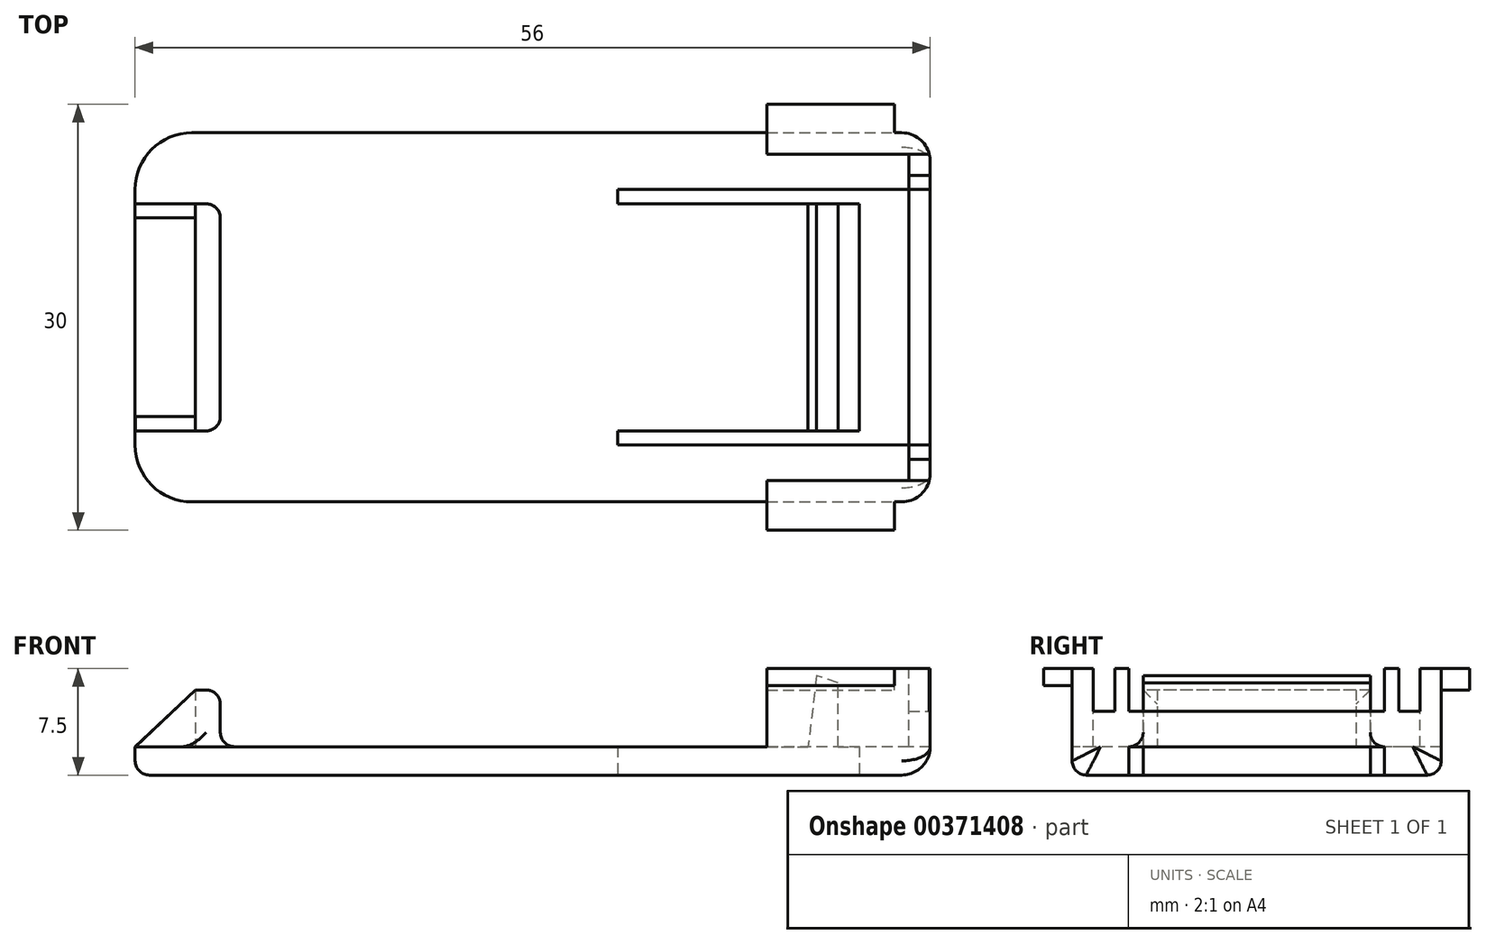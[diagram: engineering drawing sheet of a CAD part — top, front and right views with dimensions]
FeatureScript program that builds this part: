
annotation { "Feature Type Name" : "Feature", "Feature Type Description" : "" }
export const myFeature = defineFeature(function(context is Context, id is Id, definition is map)
    precondition{}
    {
        {
            var Q0;
            Q0=qCreatedBy(makeId("Top.planeOp"),FACE);
            var sketch = newSketch(context, id + "F0", { "sketchPlane" : qUnion([Q0])});
            skLineSegment(sketch, "E0.bottom", {"start": v(28, 13) * mm, "end": v(-24, 13) * mm});
            skLineSegment(sketch, "E0.top", {"start": v(28, -13) * mm, "end": v(-24, -13) * mm});
            skLineSegment(sketch, "E0.left", {"start": v(28, 13) * mm, "end": v(28, 9) * mm});
            skLineSegment(sketch, "E0.right", {"start": v(-28, 9) * mm, "end": v(-28, -9) * mm});
            skPoint(sketch, "E0.middle", {"position": v(0, 0) * mm});
            skLineSegment(sketch, "E1.bottom", {"start": v(28, 9) * mm, "end": v(6, 9) * mm});
            skLineSegment(sketch, "E1.top", {"start": v(28, -9) * mm, "end": v(6, -9) * mm});
            skLineSegment(sketch, "E1.right", {"start": v(6, 9) * mm, "end": v(6, 8) * mm});
            skLineSegment(sketch, "E2.trimOffspring", {"start": v(28, -9) * mm, "end": v(28, -13) * mm});
            skLineSegment(sketch, "E3.bottom", {"start": v(6, 8) * mm, "end": v(23, 8) * mm});
            skLineSegment(sketch, "E3.top", {"start": v(6, -8) * mm, "end": v(23, -8) * mm});
            skLineSegment(sketch, "E3.right", {"start": v(23, 8) * mm, "end": v(23, -8) * mm});
            skLineSegment(sketch, "E4.trimOffspring", {"start": v(6, -8) * mm, "end": v(6, -9) * mm});
            skPoint(sketch, "E5.visualSharp", {"position": v(-28, 13) * mm});
            skArc(sketch, "E5.filletArc", {"start": v(-24, 13) * mm, "mid": v(-26.83, 11.83) * mm, "end": v(-28, 9) * mm});
            skPoint(sketch, "E6.visualSharp", {"position": v(-28, -13) * mm});
            skArc(sketch, "E6.filletArc", {"start": v(-28, -9) * mm, "mid": v(-26.83, -11.83) * mm, "end": v(-24, -13) * mm});
            skSolve(sketch);
        }
        {
            var Q0;
            Q0=makeQuery(id+"F0.imprint","IMPRINT",FACE,{"disambiguationData":[TD([[makeQuery(id+"F0.imprint","IMPRINT",EDGE,{"derivedFrom":sQuery(id+"F0.wireOp",EDGE,"E0.bottom")}),1.0]])]});
            extrude(context, id + "F1", {"entities" : qUnion([Q0]), "depth" : 2 * mm});
        }
        {
            var Q0;
            Q0=makeQuery(id+"F1.opExtrude","CAP_FACE",FACE,{"disambiguationData":[OSD([sQuery(id+"F0.wireOp",EDGE,"E0.bottom"),sQuery(id+"F0.wireOp",EDGE,"E0.top"),sQuery(id+"F0.wireOp",EDGE,"E0.left"),sQuery(id+"F0.wireOp",EDGE,"E0.right"),sQuery(id+"F0.wireOp",EDGE,"E1.bottom"),sQuery(id+"F0.wireOp",EDGE,"E1.top"),sQuery(id+"F0.wireOp",EDGE,"E1.right"),sQuery(id+"F0.wireOp",EDGE,"E2.trimOffspring"),sQuery(id+"F0.wireOp",EDGE,"E3.bottom"),sQuery(id+"F0.wireOp",EDGE,"E3.top"),sQuery(id+"F0.wireOp",EDGE,"E3.right"),sQuery(id+"F0.wireOp",EDGE,"E4.trimOffspring"),sQuery(id+"F0.wireOp",EDGE,"E5.filletArc"),sQuery(id+"F0.wireOp",EDGE,"E6.filletArc")])],"isStart":false});
            var sketch = newSketch(context, id + "F2", { "sketchPlane" : qUnion([Q0])});
            skLineSegment(sketch, "E7.bottom", {"start": v(-23.75, 8) * mm, "end": v(-22, 8) * mm});
            skLineSegment(sketch, "E7.top", {"start": v(-23.75, -8) * mm, "end": v(-22, -8) * mm});
            skLineSegment(sketch, "E7.left", {"start": v(-23.75, 8) * mm, "end": v(-23.75, -8) * mm});
            skLineSegment(sketch, "E7.right", {"start": v(-22, 8) * mm, "end": v(-22, -8) * mm});
            skSolve(sketch);
        }
        {
            var Q0;
            Q0=makeQuery(id+"F2.imprint","IMPRINT",FACE,{"disambiguationData":[TD([[makeQuery(id+"F2.imprint","IMPRINT",EDGE,{"derivedFrom":sQuery(id+"F2.wireOp",EDGE,"E7.bottom")}),-1.0]])]});
            extrude(context, id + "F3", {"entities" : qUnion([Q0]), "operationType" : NewBodyOperationType.ADD, "depth" : 4 * mm});
        }
        {
            var Q0;
            Q0=makeQuery(id+"F3.opExtrude","SWEPT_FACE",FACE,{"disambiguationData":[OSD([sQuery(id+"F2.wireOp",EDGE,"E7.top")])]});
            var sketch = newSketch(context, id + "F4", { "sketchPlane" : qUnion([Q0])});
            skLineSegment(sketch, "E8", {"start": v(-23.75, 6) * mm, "end": v(-27.98, 2) * mm});
            skLineSegment(sketch, "E9", {"start": v(-27.98, 2) * mm, "end": v(-23.75, 2) * mm});
            skLineSegment(sketch, "E10", {"start": v(-23.75, 2) * mm, "end": v(-23.75, 6) * mm});
            skSolve(sketch);
        }
        {
            var Q0;
            Q0=makeQuery(id+"F4.imprint","IMPRINT",FACE,{"disambiguationData":[TD([[makeQuery(id+"F4.imprint","IMPRINT",EDGE,{"derivedFrom":sQuery(id+"F4.wireOp",EDGE,"E8")}),1.0]])]});
            extrude(context, id + "F5", {"entities" : qUnion([Q0]), "operationType" : NewBodyOperationType.ADD, "oppositeDirection" : true, "depth" : 1 * mm});
        }
        {
            var Q0;
            Q0=makeQuery(id+"F3.opExtrude","SWEPT_FACE",FACE,{"disambiguationData":[OSD([sQuery(id+"F2.wireOp",EDGE,"E7.bottom")])]});
            var sketch = newSketch(context, id + "F6", { "sketchPlane" : qUnion([Q0])});
            skLineSegment(sketch, "E11", {"start": v(23.75, 2) * mm, "end": v(23.75, 6) * mm});
            skLineSegment(sketch, "E12.MirrorCS", {"start": v(28, 2) * mm, "end": v(23.75, 2) * mm});
            skLineSegment(sketch, "E13.MirrorCS", {"start": v(23.75, 6) * mm, "end": v(28, 2) * mm});
            skSolve(sketch);
        }
        {
            var Q0;
            {var subQ6=sQuery(id+"F6.wireOp",EDGE,"E13.MirrorCS");Q0=makeQuery(id+"F6.imprint","IMPRINT",FACE,{"disambiguationData":[TD([[makeQuery(id+"F6.imprint","IMPRINT",EDGE,{"derivedFrom":subQ6}),-1.0]])]});}
            extrude(context, id + "F7", {"entities" : qUnion([Q0]), "operationType" : NewBodyOperationType.ADD, "oppositeDirection" : true, "depth" : 1 * mm});
        }
        {
            var Q0;
            Q0=makeQuery(id+"F1.opExtrude","SWEPT_FACE",FACE,{"disambiguationData":[OSD([sQuery(id+"F0.wireOp",EDGE,"E3.top")])]});
            var sketch = newSketch(context, id + "F8", { "sketchPlane" : qUnion([Q0])});
            skLineSegment(sketch, "E14", {"start": v(21.5, 2) * mm, "end": v(21.5, 6.5) * mm});
            skLineSegment(sketch, "E15", {"start": v(21.5, 6.5) * mm, "end": v(20, 7) * mm});
            skLineSegment(sketch, "E16", {"start": v(20, 7) * mm, "end": v(19.4, 2) * mm});
            skLineSegment(sketch, "E17", {"start": v(19.4, 2) * mm, "end": v(21.5, 2) * mm});
            skSolve(sketch);
        }
        {
            var Q0;
            Q0=makeQuery(id+"F1.opExtrude","SWEPT_FACE",FACE,{"disambiguationData":[OSD([sQuery(id+"F0.wireOp",EDGE,"E0.top")])]});
            var sketch = newSketch(context, id + "F9", { "sketchPlane" : qUnion([Q0])});
            skLineSegment(sketch, "E18.bottom", {"start": v(16.5, 2) * mm, "end": v(28, 2) * mm});
            skLineSegment(sketch, "E18.top", {"start": v(16.5, 7.5) * mm, "end": v(28, 7.5) * mm});
            skLineSegment(sketch, "E18.left", {"start": v(16.5, 2) * mm, "end": v(16.5, 7.5) * mm});
            skLineSegment(sketch, "E18.right", {"start": v(28, 2) * mm, "end": v(28, 7.5) * mm});
            skSolve(sketch);
        }
        {
            var Q0;
            Q0=makeQuery(id+"F9.imprint","IMPRINT",FACE,{"disambiguationData":[TD([[makeQuery(id+"F9.imprint","IMPRINT",EDGE,{"derivedFrom":sQuery(id+"F9.wireOp",EDGE,"E18.bottom")}),-1.0]])]});
            extrude(context, id + "F10", {"entities" : qUnion([Q0]), "operationType" : NewBodyOperationType.ADD, "oppositeDirection" : true, "depth" : 26 * mm});
        }
        {
            var Q0;
            Q0=makeQuery(id+"F10.opExtrude","SWEPT_FACE",FACE,{"disambiguationData":[OSD([sQuery(id+"F9.wireOp",EDGE,"E18.top")])]});
            var sketch = newSketch(context, id + "F11", { "sketchPlane" : qUnion([Q0])});
            skLineSegment(sketch, "E19.bottom", {"start": v(28, -11.5) * mm, "end": v(16.5, -11.5) * mm});
            skLineSegment(sketch, "E19.top", {"start": v(28, 11.5) * mm, "end": v(16.5, 11.5) * mm});
            skLineSegment(sketch, "E19.left", {"start": v(28, -11.5) * mm, "end": v(28, 11.5) * mm});
            skLineSegment(sketch, "E19.right", {"start": v(16.5, -11.5) * mm, "end": v(16.5, 11.5) * mm});
            skSolve(sketch);
        }
        {
            var Q0;
            Q0 = qSketchRegion(id + "F11", true);
            extrude(context, id + "F12", {"entities" : qUnion([Q0]), "operationType" : NewBodyOperationType.REMOVE, "oppositeDirection" : true, "depth" : 5.5 * mm});
        }
        {
            var Q0;
            Q0=makeQuery(id+"F8.imprint","IMPRINT",FACE,{"disambiguationData":[TD([[makeQuery(id+"F8.imprint","IMPRINT",EDGE,{"derivedFrom":sQuery(id+"F8.wireOp",EDGE,"E14")}),1.0]])]});
            extrude(context, id + "F13", {"entities" : qUnion([Q0]), "operationType" : NewBodyOperationType.ADD, "oppositeDirection" : true, "depth" : 16 * mm});
        }
        {
            var Q0;
            {var subQ0=sQuery(id+"F0.wireOp",EDGE,"E0.top");var subQ2=sQuery(id+"F9.wireOp",EDGE,"E18.right");var subQ10=sQuery(id+"F0.wireOp",EDGE,"E2.trimOffspring");var subQ14=sQuery(id+"F0.wireOp",EDGE,"E0.left");Q0=makeQuery(id+"F12.boolean.opBoolean","SPLIT",FACE,{"disambiguationData":[TD([makeQuery(id+"F1.opExtrude","SWEPT_FACE",FACE,{"disambiguationData":[OSD([subQ0])]})])],"derivedFrom":makeQuery(id+"F10.boolean.opBoolean","MERGE",FACE,{"derivedFrom":[makeQuery(id+"F1.opExtrude","SWEPT_FACE",FACE,{"disambiguationData":[OSD([subQ14])]}),makeQuery(id+"F1.opExtrude","SWEPT_FACE",FACE,{"disambiguationData":[OSD([subQ10])]}),makeQuery(id+"F10.opExtrude","SWEPT_FACE",FACE,{"disambiguationData":[OSD([subQ2])]})]})});}
            var sketch = newSketch(context, id + "F14", { "sketchPlane" : qUnion([Q0])});
            skLineSegment(sketch, "E20.bottom", {"start": v(-11.5, 2) * mm, "end": v(11.5, 2) * mm});
            skLineSegment(sketch, "E20.top", {"start": v(-11.5, 4.5) * mm, "end": v(-10, 4.5) * mm});
            skLineSegment(sketch, "E20.left", {"start": v(-11.5, 2) * mm, "end": v(-11.5, 4.5) * mm});
            skLineSegment(sketch, "E20.right", {"start": v(11.5, 2) * mm, "end": v(11.5, 4.5) * mm});
            skLineSegment(sketch, "E21.top", {"start": v(-10, 7.5) * mm, "end": v(-9, 7.5) * mm});
            skLineSegment(sketch, "E21.left", {"start": v(-10, 4.5) * mm, "end": v(-10, 7.5) * mm});
            skLineSegment(sketch, "E21.right", {"start": v(-9, 4.5) * mm, "end": v(-9, 7.5) * mm});
            skLineSegment(sketch, "E22.top", {"start": v(9, 7.5) * mm, "end": v(10, 7.5) * mm});
            skLineSegment(sketch, "E22.left", {"start": v(9, 4.5) * mm, "end": v(9, 7.5) * mm});
            skLineSegment(sketch, "E22.right", {"start": v(10, 4.5) * mm, "end": v(10, 7.5) * mm});
            skLineSegment(sketch, "E23.trimOffspring", {"start": v(-9, 4.5) * mm, "end": v(9, 4.5) * mm});
            skLineSegment(sketch, "E24.trimOffspring", {"start": v(10, 4.5) * mm, "end": v(11.5, 4.5) * mm});
            skSolve(sketch);
        }
        {
            var Q0;
            Q0=makeQuery(id+"F14.imprint","IMPRINT",FACE,{"disambiguationData":[TD([[makeQuery(id+"F14.imprint","IMPRINT",EDGE,{"derivedFrom":sQuery(id+"F14.wireOp",EDGE,"E20.top")}),-1.0]])]});
            extrude(context, id + "F15", {"entities" : qUnion([Q0]), "operationType" : NewBodyOperationType.ADD, "oppositeDirection" : true, "depth" : 1.5 * mm});
        }
        {
            var Q0;
            {var subQ2=sQuery(id+"F9.wireOp",EDGE,"E18.top");Q0=makeQuery(id+"F12.boolean.opBoolean","SPLIT",FACE,{"disambiguationData":[TD([makeQuery(id+"F1.opExtrude","SWEPT_FACE",FACE,{"disambiguationData":[OSD([sQuery(id+"F0.wireOp",EDGE,"E0.top")])]})])],"derivedFrom":makeQuery(id+"F10.opExtrude","SWEPT_FACE",FACE,{"disambiguationData":[OSD([subQ2])]})});}
            var sketch = newSketch(context, id + "F16", { "sketchPlane" : qUnion([Q0])});
            skLineSegment(sketch, "E25.bottom", {"start": v(16.5, -11.5) * mm, "end": v(25.5, -11.5) * mm});
            skLineSegment(sketch, "E25.top", {"start": v(16.5, -15) * mm, "end": v(25.5, -15) * mm});
            skLineSegment(sketch, "E25.left", {"start": v(16.5, -11.5) * mm, "end": v(16.5, -15) * mm});
            skLineSegment(sketch, "E25.right", {"start": v(25.5, -11.5) * mm, "end": v(25.5, -15) * mm});
            skSolve(sketch);
        }
        {
            var Q0;
            {var subQ0=sQuery(id+"F16.wireOp",EDGE,"E25.top");Q0=makeQuery(id+"F16.imprint","IMPRINT",FACE,{"disambiguationData":[TD([[makeQuery(id+"F16.imprint","IMPRINT",EDGE,{"derivedFrom":subQ0}),1.0]])]});}
            extrude(context, id + "F17", {"entities" : qUnion([Q0]), "operationType" : NewBodyOperationType.ADD, "oppositeDirection" : true, "depth" : 1.2 * mm});
        }
        {
            var Q0;
            {var subQ2=sQuery(id+"F9.wireOp",EDGE,"E18.top");Q0=makeQuery(id+"F12.boolean.opBoolean","SPLIT",FACE,{"disambiguationData":[TD([makeQuery(id+"F1.opExtrude","SWEPT_FACE",FACE,{"disambiguationData":[OSD([sQuery(id+"F0.wireOp",EDGE,"E0.bottom")])]})])],"derivedFrom":makeQuery(id+"F10.opExtrude","SWEPT_FACE",FACE,{"disambiguationData":[OSD([subQ2])]})});}
            var sketch = newSketch(context, id + "F18", { "sketchPlane" : qUnion([Q0])});
            skLineSegment(sketch, "E26.bottom", {"start": v(16.5, 11.5) * mm, "end": v(25.5, 11.5) * mm});
            skLineSegment(sketch, "E26.top", {"start": v(16.5, 15) * mm, "end": v(25.5, 15) * mm});
            skLineSegment(sketch, "E26.left", {"start": v(16.5, 11.5) * mm, "end": v(16.5, 15) * mm});
            skLineSegment(sketch, "E26.right", {"start": v(25.5, 11.5) * mm, "end": v(25.5, 15) * mm});
            skSolve(sketch);
        }
        {
            var Q0;
            {var subQ0=sQuery(id+"F18.wireOp",EDGE,"E26.top");Q0=makeQuery(id+"F18.imprint","IMPRINT",FACE,{"disambiguationData":[TD([[makeQuery(id+"F18.imprint","IMPRINT",EDGE,{"derivedFrom":subQ0}),-1.0]])]});}
            extrude(context, id + "F19", {"entities" : qUnion([Q0]), "operationType" : NewBodyOperationType.ADD, "oppositeDirection" : true, "depth" : 1.5 * mm});
        }
        {
            var Q0;
            Q0=makeQuery(id+"F1.opExtrude","CAP_EDGE",EDGE,{"disambiguationData":[OSD([sQuery(id+"F0.wireOp",EDGE,"E0.right")])],"isStart":true});
            fillet(context, id + "F20", {"entities" : qUnion([Q0]), "radius" : 1 * mm, "tangentPropagation" : true, "allowEdgeOverflow" : false});
        }
        {
            var Q0;
            Q0=makeQuery(id+"F1.opExtrude","CAP_EDGE",EDGE,{"disambiguationData":[OSD([sQuery(id+"F0.wireOp",EDGE,"E2.trimOffspring")])],"isStart":true});
            var Q1;
            Q1=makeQuery(id+"F1.opExtrude","CAP_EDGE",EDGE,{"disambiguationData":[OSD([sQuery(id+"F0.wireOp",EDGE,"E0.left")])],"isStart":true});
            fillet(context, id + "F21", {"entities" : qUnion([Q0, Q1]), "radius" : 2 * mm, "tangentPropagation" : true, "allowEdgeOverflow" : false});
        }
        {
            var Q0;
            Q0=makeQuery(id+"F3.opExtrude","SWEPT_FACE",FACE,{"disambiguationData":[OSD([sQuery(id+"F2.wireOp",EDGE,"E7.right")])]});
            fillet(context, id + "F22", {"entities" : qUnion([Q0]), "radius" : 1 * mm, "tangentPropagation" : true, "allowEdgeOverflow" : false});
        }
    });
